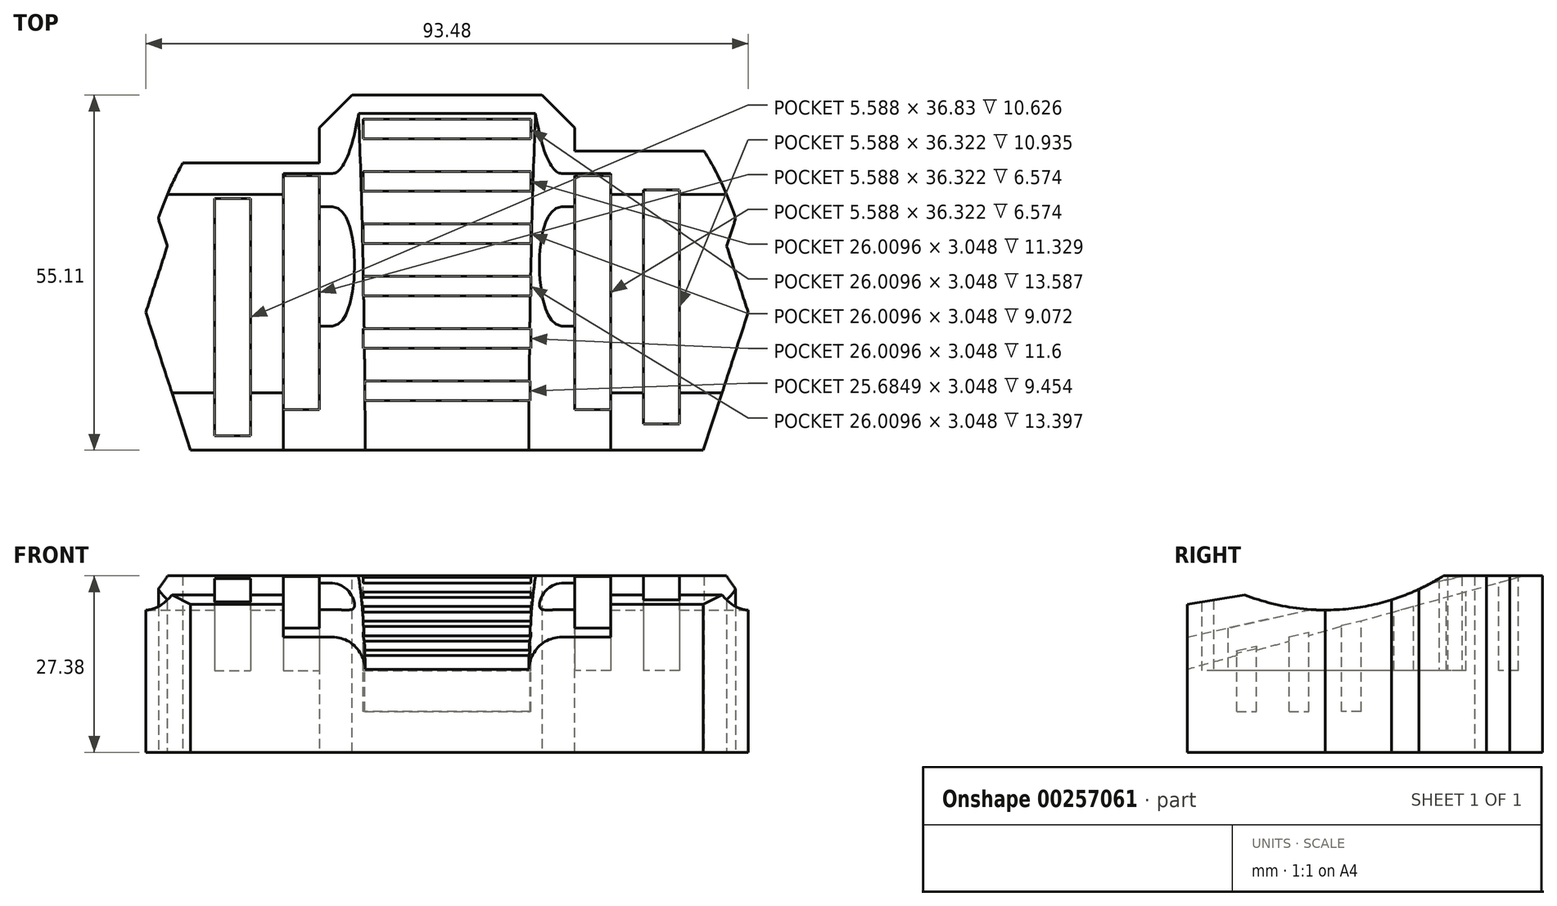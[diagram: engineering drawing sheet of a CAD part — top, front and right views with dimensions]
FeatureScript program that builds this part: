
annotation { "Feature Type Name" : "Feature", "Feature Type Description" : "" }
export const myFeature = defineFeature(function(context is Context, id is Id, definition is map)
    precondition{}
    {
        {
            var Q0;
            Q0=qCreatedBy(makeId("Top.planeOp"),FACE);
            var sketch = newSketch(context, id + "F0", { "sketchPlane" : qUnion([Q0])});
            skCircle(sketch, "E0.cCircle", {"center": v(0, 0) * mm, "radius": 44.45 * mm, "construction": true});
            skLineSegment(sketch, "E0.1", {"start": v(-14.44, -44.45) * mm, "end": v(-37.81, -27.47) * mm});
            skLineSegment(sketch, "E0.2", {"start": v(-37.81, -27.47) * mm, "end": v(-46.74, 0) * mm});
            skLineSegment(sketch, "E0.3", {"start": v(-46.74, 0) * mm, "end": v(-38.45, 25.5) * mm});
            skLineSegment(sketch, "E0.5", {"start": v(-14.44, 44.45) * mm, "end": v(14.44, 44.45) * mm});
            skLineSegment(sketch, "E0.7", {"start": v(37.81, 27.47) * mm, "end": v(46.74, 0) * mm});
            skLineSegment(sketch, "E0.8", {"start": v(46.74, 0) * mm, "end": v(37.81, -27.47) * mm});
            skLineSegment(sketch, "E0.9", {"start": v(37.81, -27.47) * mm, "end": v(14.44, -44.45) * mm});
            skPoint(sketch, "E0.0.midPoint", {"position": v(0, -44.45) * mm});
            skCircle(sketch, "E1.cCircle", {"center": v(0, 0) * mm, "radius": 38.1 * mm, "construction": true});
            skLineSegment(sketch, "E1.0", {"start": v(27.68, -38.1) * mm, "end": v(-27.68, -38.1) * mm});
            skLineSegment(sketch, "E1.1", {"start": v(-27.68, -38.1) * mm, "end": v(-44.79, 14.55) * mm});
            skLineSegment(sketch, "E1.2", {"start": v(-44.79, 14.55) * mm, "end": v(0, 47.1) * mm});
            skLineSegment(sketch, "E1.3", {"start": v(0, 47.1) * mm, "end": v(44.79, 14.55) * mm});
            skLineSegment(sketch, "E1.4", {"start": v(44.79, 14.55) * mm, "end": v(27.68, -38.1) * mm});
            skPoint(sketch, "E1.0.midPoint", {"position": v(0, -38.1) * mm});
            skArc(sketch, "E2", {"start": v(-27.68, -38.1) * mm, "mid": v(0, -47.1) * mm, "end": v(27.68, -38.1) * mm});
            skArc(sketch, "E3.trimOffspring", {"start": v(44.79, 14.55) * mm, "mid": v(0, 47.1) * mm, "end": v(-44.79, 14.55) * mm});
            skSolve(sketch);
        }
        {
            var Q0;
            Q0 = qSketchRegion(id + "F0", true);
            extrude(context, id + "F1", {"entities" : qUnion([Q0]), "depth" : 50.8 * mm, "hasSecondDirection" : true, "secondDirectionOppositeDirection" : false, "secondDirectionDepth" : 19.05 * mm});
        }
        {
            var Q0;
            Q0=qCreatedBy(makeId("Right.planeOp"),FACE);
            var sketch = newSketch(context, id + "F2", { "sketchPlane" : qUnion([Q0])});
            skLineSegment(sketch, "E4.bottom", {"start": v(69.46, 57.15) * mm, "end": v(-44.84, 57.15) * mm});
            skLineSegment(sketch, "E4.right", {"start": v(-44.84, 57.15) * mm, "end": v(-44.84, 25.4) * mm});
            skLineSegment(sketch, "E5", {"start": v(69.46, 57.15) * mm, "end": v(-44.84, 25.4) * mm});
            skSolve(sketch);
        }
        {
            var Q0;
            Q0 = qSketchRegion(id + "F2", true);
            extrude(context, id + "F3", {"entities" : qUnion([Q0]), "operationType" : NewBodyOperationType.REMOVE, "endBound" : BoundingType.SYMMETRIC, "oppositeDirection" : true, "depth" : 25.4 * mm});
        }
        {
            var Q0;
            Q0=qCreatedBy(makeId("Right.planeOp"),FACE);
            var sketch = newSketch(context, id + "F4", { "sketchPlane" : qUnion([Q0])});
            skLineSegment(sketch, "E6.bottom", {"start": v(70.07, 57.15) * mm, "end": v(-44.84, 57.15) * mm});
            skLineSegment(sketch, "E6.right", {"start": v(-44.84, 57.15) * mm, "end": v(-44.84, 31.75) * mm});
            skLineSegment(sketch, "E7", {"start": v(-44.84, 31.75) * mm, "end": v(70.07, 57.15) * mm});
            skSolve(sketch);
        }
        {
            var Q0;
            Q0 = qSketchRegion(id + "F4", true);
            extrude(context, id + "F5", {"entities" : qUnion([Q0]), "operationType" : NewBodyOperationType.REMOVE, "endBound" : BoundingType.SYMMETRIC, "oppositeDirection" : true, "depth" : 50.8 * mm});
        }
        {
            var Q0;
            Q0=qCreatedBy(makeId("Right.planeOp"),FACE);
            var sketch = newSketch(context, id + "F6", { "sketchPlane" : qUnion([Q0])});
            skLineSegment(sketch, "E8.bottom", {"start": v(-44.84, 57.15) * mm, "end": v(69.46, 57.15) * mm});
            skLineSegment(sketch, "E8.left", {"start": v(-44.84, 57.15) * mm, "end": v(-44.84, 38.1) * mm});
            skLineSegment(sketch, "E9", {"start": v(-44.84, 38.1) * mm, "end": v(69.46, 57.15) * mm});
            skLineSegment(sketch, "E10.top", {"start": v(48.46, 46.43) * mm, "end": v(5.12, 46.43) * mm});
            skLineSegment(sketch, "E10.left", {"start": v(48.46, 53.65) * mm, "end": v(48.46, 46.43) * mm});
            skSolve(sketch);
        }
        {
            var Q0;
            Q0 = qSketchRegion(id + "F6", true);
            extrude(context, id + "F7", {"entities" : qUnion([Q0]), "operationType" : NewBodyOperationType.REMOVE, "endBound" : BoundingType.SYMMETRIC, "oppositeDirection" : true, "depth" : 101.6 * mm});
        }
        {
            var Q0;
            Q0=makeQuery(id+"F5.boolean.opBoolean","INTERSECT",EDGE,{"disambiguationData":[OD(1.0)],"derivedFrom":[makeQuery(id+"F1.opExtrude","SWEPT_FACE",FACE,{"disambiguationData":[OSD([sQuery(id+"F0.wireOp",EDGE,"E2")])]}),makeQuery(id+"F5.opExtrude","SWEPT_FACE",FACE,{"disambiguationData":[OSD([sQuery(id+"F4.wireOp",EDGE,"E7")])]})]});
            var Q1;
            Q1=makeQuery(id+"F5.boolean.opBoolean","INTERSECT",EDGE,{"disambiguationData":[OD(0.0)],"derivedFrom":[makeQuery(id+"F1.opExtrude","SWEPT_FACE",FACE,{"disambiguationData":[OSD([sQuery(id+"F0.wireOp",EDGE,"E2")])]}),makeQuery(id+"F5.opExtrude","SWEPT_FACE",FACE,{"disambiguationData":[OSD([sQuery(id+"F4.wireOp",EDGE,"E7")])]})]});
            var Q2;
            Q2=makeQuery(id+"F3.boolean.opBoolean","INTERSECT",EDGE,{"derivedFrom":[makeQuery(id+"F1.opExtrude","SWEPT_FACE",FACE,{"disambiguationData":[OSD([sQuery(id+"F0.wireOp",EDGE,"E3.trimOffspring")])]}),makeQuery(id+"F3.opExtrude","SWEPT_FACE",FACE,{"disambiguationData":[OSD([sQuery(id+"F2.wireOp",EDGE,"E5")])]})]});
            fillet(context, id + "F8", {"entities" : qUnion([Q0, Q1, Q2]), "radius" : 12.7 * mm, "tangentPropagation" : true, "allowEdgeOverflow" : false});
        }
        {
            var Q0;
            Q0=qCreatedBy(makeId("Top.planeOp"),FACE);
            cPlane(context, id + "F9", {"entities" : qUnion([Q0]), "cplaneType" : CPlaneType.OFFSET, "offset" : 50.8 * mm, "width" : 152.4 * mm, "height" : 152.4 * mm});
        }
        {
            var Q0;
            Q0=makeQuery(id+"F5.boolean.opBoolean","INTERSECT",EDGE,{"derivedFrom":[makeQuery(id+"F3.boolean.opBoolean","COPY",FACE,{"derivedFrom":makeQuery(id+"F3.opExtrude","CAP_FACE",FACE,{"disambiguationData":[OSD([sQuery(id+"F2.wireOp",EDGE,"E4.bottom"),sQuery(id+"F2.wireOp",EDGE,"E4.right"),sQuery(id+"F2.wireOp",EDGE,"E5")])],"isStart":false})}),makeQuery(id+"F5.opExtrude","SWEPT_FACE",FACE,{"disambiguationData":[OSD([sQuery(id+"F4.wireOp",EDGE,"E7")])]})]});
            var Q1;
            Q1=makeQuery(id+"F5.boolean.opBoolean","INTERSECT",EDGE,{"derivedFrom":[makeQuery(id+"F3.boolean.opBoolean","COPY",FACE,{"derivedFrom":makeQuery(id+"F3.opExtrude","CAP_FACE",FACE,{"disambiguationData":[OSD([sQuery(id+"F2.wireOp",EDGE,"E4.bottom"),sQuery(id+"F2.wireOp",EDGE,"E4.right"),sQuery(id+"F2.wireOp",EDGE,"E5")])],"isStart":true})}),makeQuery(id+"F5.opExtrude","SWEPT_FACE",FACE,{"disambiguationData":[OSD([sQuery(id+"F4.wireOp",EDGE,"E7")])]})]});
            fillet(context, id + "F10", {"entities" : qUnion([Q0, Q1]), "radius" : 5.08 * mm, "tangentPropagation" : true, "allowEdgeOverflow" : false});
        }
        {
            var Q0;
            Q0=qCreatedBy(id+"F9.planeOp",FACE);
            var sketch = newSketch(context, id + "F11", { "sketchPlane" : qUnion([Q0])});
            skLineSegment(sketch, "E11.bottom", {"start": v(-36.07, 17.64) * mm, "end": v(-30.48, 17.64) * mm});
            skLineSegment(sketch, "E11.top", {"start": v(-36.07, -19.19) * mm, "end": v(-30.48, -19.19) * mm});
            skLineSegment(sketch, "E11.left", {"start": v(-36.07, 17.64) * mm, "end": v(-36.07, -19.19) * mm});
            skLineSegment(sketch, "E11.right", {"start": v(-30.48, 17.64) * mm, "end": v(-30.48, -19.19) * mm});
            skLineSegment(sketch, "E12.bottom", {"start": v(-25.4, 21.22) * mm, "end": v(-19.81, 21.22) * mm});
            skLineSegment(sketch, "E12.top", {"start": v(-25.4, -15.1) * mm, "end": v(-19.81, -15.1) * mm});
            skLineSegment(sketch, "E12.left", {"start": v(-25.4, 21.22) * mm, "end": v(-25.4, -15.1) * mm});
            skLineSegment(sketch, "E12.right", {"start": v(-19.81, 21.22) * mm, "end": v(-19.81, -15.1) * mm});
            skLineSegment(sketch, "E13.bottom", {"start": v(36.07, 18.98) * mm, "end": v(30.48, 18.98) * mm});
            skLineSegment(sketch, "E13.top", {"start": v(36.07, -17.34) * mm, "end": v(30.48, -17.34) * mm});
            skLineSegment(sketch, "E13.left", {"start": v(36.07, 18.98) * mm, "end": v(36.07, -17.34) * mm});
            skLineSegment(sketch, "E13.right", {"start": v(30.48, 18.98) * mm, "end": v(30.48, -17.34) * mm});
            skLineSegment(sketch, "E14.bottom", {"start": v(25.4, 21.22) * mm, "end": v(19.81, 21.22) * mm});
            skLineSegment(sketch, "E14.top", {"start": v(25.4, -15.1) * mm, "end": v(19.81, -15.1) * mm});
            skLineSegment(sketch, "E14.left", {"start": v(25.4, 21.22) * mm, "end": v(25.4, -15.1) * mm});
            skLineSegment(sketch, "E14.right", {"start": v(19.81, 21.22) * mm, "end": v(19.81, -15.1) * mm});
            skSolve(sketch);
        }
        {
            var Q0;
            Q0 = qSketchRegion(id + "F11", true);
            extrude(context, id + "F12", {"entities" : qUnion([Q0]), "operationType" : NewBodyOperationType.REMOVE, "depth" : 25.4 * mm, "hasSecondDirection" : true, "secondDirectionOppositeDirection" : true, "secondDirectionDepth" : 19.05 * mm});
        }
        {
            var Q0;
            Q0=qCreatedBy(id+"F9.planeOp",FACE);
            var sketch = newSketch(context, id + "F13", { "sketchPlane" : qUnion([Q0])});
            skLineSegment(sketch, "E15.bottom", {"start": v(13, 13.72) * mm, "end": v(-13, 13.72) * mm});
            skLineSegment(sketch, "E15.left", {"start": v(13, 13.72) * mm, "end": v(13, 10.67) * mm});
            skLineSegment(sketch, "E16", {"start": v(-13, 10.67) * mm, "end": v(13, 10.67) * mm});
            skLineSegment(sketch, "E17", {"start": v(-13, 29.98) * mm, "end": v(13, 29.98) * mm});
            skLineSegment(sketch, "E18", {"start": v(13, 26.93) * mm, "end": v(-13, 26.93) * mm});
            skLineSegment(sketch, "E19", {"start": v(-13, 21.85) * mm, "end": v(13, 21.85) * mm});
            skLineSegment(sketch, "E20", {"start": v(13, 18.8) * mm, "end": v(-13, 18.8) * mm});
            skLineSegment(sketch, "E21.trimOffspring", {"start": v(13, 29.98) * mm, "end": v(13, 26.93) * mm});
            skLineSegment(sketch, "E22.trimOffspring", {"start": v(13, 21.85) * mm, "end": v(13, 18.8) * mm});
            skLineSegment(sketch, "E23", {"start": v(-13, 29.98) * mm, "end": v(-13, 26.93) * mm});
            skLineSegment(sketch, "E24", {"start": v(-13, 21.85) * mm, "end": v(-13, 18.8) * mm});
            skLineSegment(sketch, "E25", {"start": v(-13, 13.72) * mm, "end": v(-13, 10.67) * mm});
            skSolve(sketch);
        }
        {
            var Q0;
            Q0 = qSketchRegion(id + "F13", true);
            extrude(context, id + "F14", {"entities" : qUnion([Q0]), "operationType" : NewBodyOperationType.REMOVE, "oppositeDirection" : true, "depth" : 19.05 * mm});
        }
        {
            var Q0;
            Q0=qCreatedBy(id+"F9.planeOp",FACE);
            var sketch = newSketch(context, id + "F15", { "sketchPlane" : qUnion([Q0])});
            skLineSegment(sketch, "E26.bottom", {"start": v(13, -5.58) * mm, "end": v(-13, -5.58) * mm});
            skLineSegment(sketch, "E26.top", {"start": v(13, -2.54) * mm, "end": v(-13, -2.54) * mm});
            skLineSegment(sketch, "E26.left", {"start": v(13, -5.58) * mm, "end": v(13, -2.54) * mm});
            skLineSegment(sketch, "E26.right", {"start": v(-13, -5.58) * mm, "end": v(-13, -2.54) * mm});
            skLineSegment(sketch, "E27.MirrorCS", {"start": v(-12.8, -13.71) * mm, "end": v(-12.8, -10.66) * mm});
            skLineSegment(sketch, "E28.MirrorCS", {"start": v(-13.12, -10.66) * mm, "end": v(12.9, -10.66) * mm});
            skLineSegment(sketch, "E29.MirrorCS", {"start": v(-13.12, -13.71) * mm, "end": v(12.9, -13.71) * mm});
            skLineSegment(sketch, "E30.bottom", {"start": v(13, 5.6) * mm, "end": v(-13, 5.6) * mm});
            skLineSegment(sketch, "E30.top", {"start": v(13, 2.54) * mm, "end": v(-13, 2.54) * mm});
            skLineSegment(sketch, "E30.left", {"start": v(13, 5.6) * mm, "end": v(13, 2.54) * mm});
            skLineSegment(sketch, "E30.right", {"start": v(-13, 5.6) * mm, "end": v(-13, 2.54) * mm});
            skLineSegment(sketch, "E31", {"start": v(12.9, -13.71) * mm, "end": v(12.9, -10.66) * mm});
            skSolve(sketch);
        }
        {
            var Q0;
            Q0 = qSketchRegion(id + "F15", true);
            extrude(context, id + "F16", {"entities" : qUnion([Q0]), "operationType" : NewBodyOperationType.REMOVE, "oppositeDirection" : true, "depth" : 25.4 * mm});
        }
        {
            var Q0;
            Q0=qCreatedBy(makeId("Right.planeOp"),FACE);
            var sketch = newSketch(context, id + "F17", { "sketchPlane" : qUnion([Q0])});
            skCircle(sketch, "E32", {"center": v(0, 75.5) * mm, "radius": 34.37 * mm});
            skSolve(sketch);
        }
        {
            var Q0;
            Q0 = qSketchRegion(id + "F17", true);
            extrude(context, id + "F18", {"entities" : qUnion([Q0]), "operationType" : NewBodyOperationType.REMOVE, "endBound" : BoundingType.SYMMETRIC, "oppositeDirection" : true, "depth" : 127 * mm});
        }
        {
            var Q0;
            Q0=qCreatedBy(id+"F9.planeOp",FACE);
            var sketch = newSketch(context, id + "F19", { "sketchPlane" : qUnion([Q0])});
            skLineSegment(sketch, "E33.bottom", {"start": v(46.89, -21.4) * mm, "end": v(-54.71, -21.4) * mm});
            skLineSegment(sketch, "E33.top", {"start": v(46.89, -53.44) * mm, "end": v(-54.71, -53.44) * mm});
            skLineSegment(sketch, "E33.left", {"start": v(46.89, -21.4) * mm, "end": v(46.89, -53.44) * mm});
            skLineSegment(sketch, "E33.right", {"start": v(-54.71, -21.4) * mm, "end": v(-54.71, -53.44) * mm});
            skLineSegment(sketch, "E34.bottom", {"start": v(-54.71, 51.88) * mm, "end": v(46.89, 51.88) * mm});
            skLineSegment(sketch, "E34.top", {"start": v(-54.71, 33.71) * mm, "end": v(46.89, 33.71) * mm});
            skLineSegment(sketch, "E34.left", {"start": v(-54.71, 51.88) * mm, "end": v(-54.71, 33.71) * mm});
            skLineSegment(sketch, "E34.right", {"start": v(46.89, 51.88) * mm, "end": v(46.89, 33.71) * mm});
            skLineSegment(sketch, "E35.bottom", {"start": v(40.54, 41.56) * mm, "end": v(19.81, 41.56) * mm});
            skLineSegment(sketch, "E35.top", {"start": v(40.54, 25.04) * mm, "end": v(19.81, 25.04) * mm});
            skLineSegment(sketch, "E35.left", {"start": v(40.54, 41.56) * mm, "end": v(40.54, 25.04) * mm});
            skLineSegment(sketch, "E35.right", {"start": v(19.81, 41.56) * mm, "end": v(19.81, 25.04) * mm});
            skLineSegment(sketch, "E36.bottom", {"start": v(-19.81, 40.32) * mm, "end": v(-48.36, 40.32) * mm});
            skLineSegment(sketch, "E36.top", {"start": v(-19.81, 23.19) * mm, "end": v(-48.36, 23.19) * mm});
            skLineSegment(sketch, "E36.left", {"start": v(-19.81, 40.32) * mm, "end": v(-19.81, 23.19) * mm});
            skLineSegment(sketch, "E36.right", {"start": v(-48.36, 40.32) * mm, "end": v(-48.36, 23.19) * mm});
            skSolve(sketch);
        }
        {
            var Q0;
            Q0 = qSketchRegion(id + "F19", true);
            extrude(context, id + "F20", {"entities" : qUnion([Q0]), "operationType" : NewBodyOperationType.REMOVE, "endBound" : BoundingType.SYMMETRIC, "oppositeDirection" : true, "depth" : 76.2 * mm});
        }
        {
            var Q0;
            Q0=makeQuery(id+"F20.boolean.opBoolean","COPY",EDGE,{"derivedFrom":makeQuery(id+"F20.opExtrude","SWEPT_EDGE",EDGE,{"disambiguationData":[OSD([sQuery(id+"F19.wireOp",EDGE,"E34.top"),sQuery(id+"F19.wireOp",EDGE,"E36.left")])]})});
            var Q1;
            Q1=makeQuery(id+"F20.boolean.opBoolean","COPY",EDGE,{"derivedFrom":makeQuery(id+"F20.opExtrude","SWEPT_EDGE",EDGE,{"disambiguationData":[OSD([sQuery(id+"F19.wireOp",EDGE,"E34.top"),sQuery(id+"F19.wireOp",EDGE,"E35.right")])]})});
            chamfer(context, id + "F21", {"entities" : qUnion([Q0, Q1]), "width" : 5.08 * mm, "tangentPropagation" : true});
        }
    });
